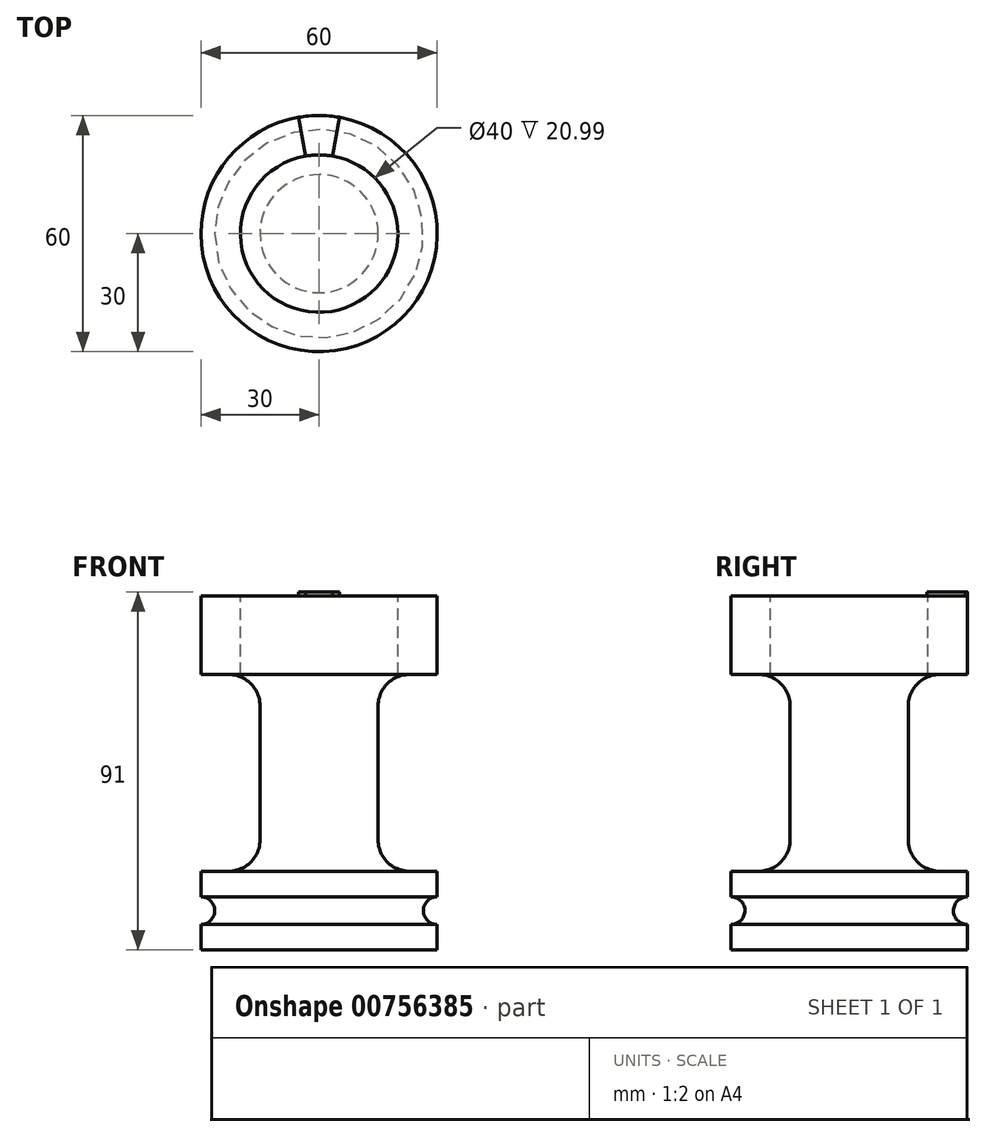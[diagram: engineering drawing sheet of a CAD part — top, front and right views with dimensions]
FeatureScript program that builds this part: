
annotation { "Feature Type Name" : "Feature", "Feature Type Description" : "" }
export const myFeature = defineFeature(function(context is Context, id is Id, definition is map)
    precondition{}
    {
        {
            var Q0;
            Q0=qCreatedBy(makeId("Front.planeOp"),FACE);
            var sketch = newSketch(context, id + "F0", { "sketchPlane" : qUnion([Q0])});
            skLineSegment(sketch, "E0.bottom", {"start": v(0, 0) * mm, "end": v(30, 0) * mm});
            skLineSegment(sketch, "E0.top", {"start": v(0, 90) * mm, "end": v(30, 90) * mm});
            skLineSegment(sketch, "E0.left", {"start": v(0, 0) * mm, "end": v(0, 90) * mm});
            skLineSegment(sketch, "E0.right", {"start": v(30, 0) * mm, "end": v(30, 6.5) * mm});
            skLineSegment(sketch, "E1.top", {"start": v(30, 20) * mm, "end": v(15, 20) * mm});
            skLineSegment(sketch, "E2.top", {"start": v(30, 70) * mm, "end": v(15, 70) * mm});
            skLineSegment(sketch, "E3.trimOffspring", {"start": v(30, 70) * mm, "end": v(30, 90) * mm});
            skLineSegment(sketch, "E4", {"start": v(15, 20) * mm, "end": v(15, 70) * mm});
            skArc(sketch, "E5", {"start": v(30, 13.5) * mm, "mid": v(26.5, 10) * mm, "end": v(30, 6.5) * mm});
            skLineSegment(sketch, "E6.trimOffspring", {"start": v(30, 13.5) * mm, "end": v(30, 20) * mm});
            skSolve(sketch);
        }
        {
            var Q0;
            Q0=makeQuery(id+"F0.imprint","IMPRINT",FACE,{"disambiguationData":[TD([[makeQuery(id+"F0.imprint","IMPRINT",EDGE,{"derivedFrom":sQuery(id+"F0.wireOp",EDGE,"E0.bottom")}),1.0]])]});
            var Q1;
            Q1=sQuery(id+"F0.wireOp",EDGE,"E0.left");
            revolve(context, id + "F1", {"surfaceOperationType" : NewSurfaceOperationType.NEW, "entities" : qUnion([Q0]), "axis" : qUnion([Q1]), "revolveType" : RevolveType.FULL});
        }
        {
            var Q0;
            Q0=makeQuery(id+"F1.opRevolve","SWEPT_FACE",FACE,{"disambiguationData":[OSD([sQuery(id+"F0.wireOp",EDGE,"E0.top")])]});
            var sketch = newSketch(context, id + "F2", { "sketchPlane" : qUnion([Q0])});
            skCircle(sketch, "E7", {"center": v(0, 0) * mm, "radius": 30 * mm});
            skCircle(sketch, "E8.0", {"center": v(0, 0) * mm, "radius": 20 * mm});
            skLineSegment(sketch, "E9", {"start": v(3.47, 19.7) * mm, "end": v(5.2, 29.54) * mm});
            skLineSegment(sketch, "E10", {"start": v(-3.47, 19.7) * mm, "end": v(-5.2, 29.54) * mm});
            skLineSegment(sketch, "E11", {"start": v(19.7, 3.47) * mm, "end": v(29.54, 5.2) * mm});
            skLineSegment(sketch, "E12", {"start": v(19.7, -3.47) * mm, "end": v(29.54, -5.2) * mm});
            skSolve(sketch);
        }
        {
            var Q0;
            Q0=makeQuery(id+"F2.imprint","IMPRINT",FACE,{"disambiguationData":[TD([[makeQuery(id+"F2.imprint","IMPRINT",EDGE,{"derivedFrom":sQuery(id+"F2.wireOp",EDGE,"E8.0")}),1.0]])]});
            extrude(context, id + "F3", {"entities" : qUnion([Q0]), "operationType" : NewBodyOperationType.REMOVE, "oppositeDirection" : true, "depth" : 19.99 * mm, "offsetDistance" : 25 * mm});
        }
        {
            var Q0;
            Q0=makeQuery(id+"F1.opRevolve","SWEPT_FACE",FACE,{"disambiguationData":[OSD([sQuery(id+"F0.wireOp",EDGE,"E4")])]});
            fillet(context, id + "F4", {"entities" : qUnion([Q0]), "radius" : 8 * mm, "tangentPropagation" : true, "allowEdgeOverflow" : false});
        }
        {
            var Q0;
            {var subQ0=sQuery(id+"F2.wireOp",EDGE,"E9");Q0=makeQuery(id+"F2.imprint","IMPRINT",FACE,{"disambiguationData":[TD([[makeQuery(id+"F2.imprint","IMPRINT",EDGE,{"derivedFrom":subQ0}),1.0]])]});}
            extrude(context, id + "F5", {"entities" : qUnion([Q0]), "operationType" : NewBodyOperationType.ADD, "depth" : 1 * mm, "offsetDistance" : 25 * mm});
        }
    });
